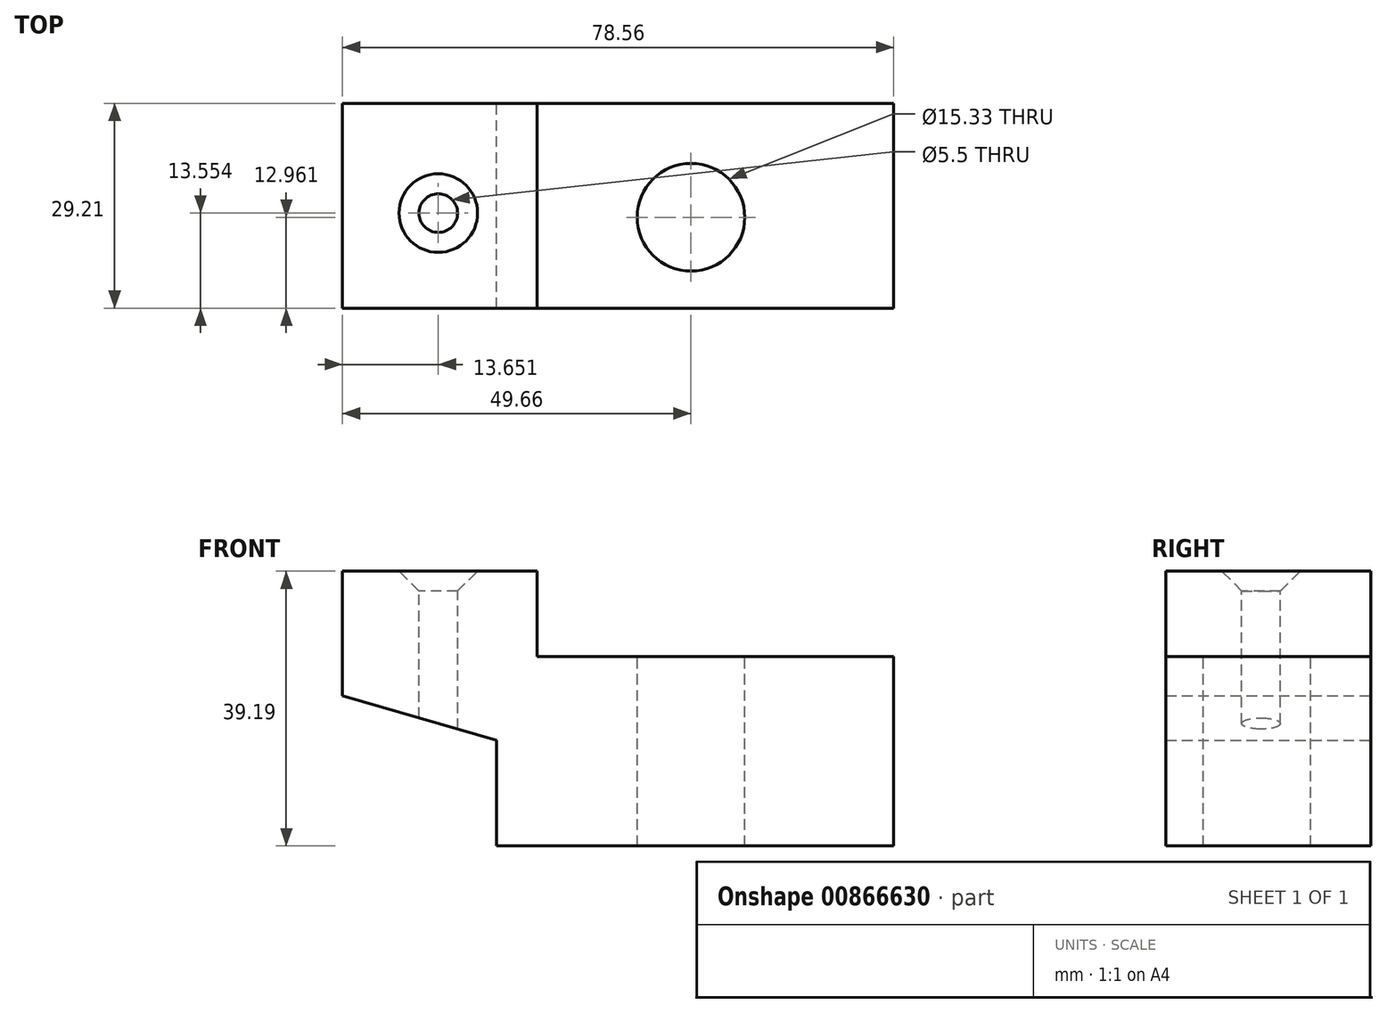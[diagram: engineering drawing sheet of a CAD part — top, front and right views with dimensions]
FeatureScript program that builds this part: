
annotation { "Feature Type Name" : "Feature", "Feature Type Description" : "" }
export const myFeature = defineFeature(function(context is Context, id is Id, definition is map)
    precondition{}
    {
        {
            var Q0;
            Q0=qCreatedBy(makeId("Front.planeOp"),FACE);
            var sketch = newSketch(context, id + "F0", { "sketchPlane" : qUnion([Q0])});
            skLineSegment(sketch, "E0", {"start": v(-42, 8.07) * mm, "end": v(-42, 25.85) * mm});
            skLineSegment(sketch, "E1", {"start": v(-42, 25.85) * mm, "end": v(-14.24, 25.85) * mm});
            skLineSegment(sketch, "E2", {"start": v(-14.24, 25.85) * mm, "end": v(-14.24, 13.7) * mm});
            skLineSegment(sketch, "E3", {"start": v(-14.24, 13.7) * mm, "end": v(36.56, 13.7) * mm});
            skLineSegment(sketch, "E4", {"start": v(36.56, 13.7) * mm, "end": v(36.56, -13.34) * mm});
            skLineSegment(sketch, "E5", {"start": v(36.56, -13.34) * mm, "end": v(-20.05, -13.34) * mm});
            skLineSegment(sketch, "E6", {"start": v(-20.05, -13.34) * mm, "end": v(-20.05, 1.72) * mm});
            skLineSegment(sketch, "E7", {"start": v(-20.05, 1.72) * mm, "end": v(-42, 8.07) * mm});
            skSolve(sketch);
        }
        {
            var Q0;
            Q0 = qSketchRegion(id + "F0", true);
            extrude(context, id + "F1", {"entities" : qUnion([Q0]), "depth" : 29.2 * mm, "offsetDistance" : 25.4 * mm});
        }
        {
            var Q0;
            Q0=makeQuery(id+"F1.opExtrude","SWEPT_FACE",FACE,{"disambiguationData":[OSD([sQuery(id+"F0.wireOp",EDGE,"E3")])]});
            var sketch = newSketch(context, id + "F2", { "sketchPlane" : qUnion([Q0])});
            skCircle(sketch, "E8", {"center": v(7.66, -16.25) * mm, "radius": 7.66 * mm});
            skSolve(sketch);
        }
        {
            var Q0;
            Q0 = qSketchRegion(id + "F2", true);
            extrude(context, id + "F3", {"entities" : qUnion([Q0]), "operationType" : NewBodyOperationType.REMOVE, "oppositeDirection" : true, "depth" : 41.4 * mm, "offsetDistance" : 25.4 * mm});
        }
        {
            var Q0;
            Q0=makeQuery(id+"F1.opExtrude","SWEPT_FACE",FACE,{"disambiguationData":[OSD([sQuery(id+"F0.wireOp",EDGE,"E1")])]});
            var sketch = newSketch(context, id + "F4", { "sketchPlane" : qUnion([Q0])});
            skPoint(sketch, "E9", {"position": v(-28.35, -15.66) * mm});
            skSolve(sketch);
        }
        {
            var Q0;
            Q0=sQuery(id+"F4.wireOp",VERTEX,"E9");
            var Q1;
            Q1=makeQuery(id+"F1.opExtrude","SWEPT_BODY",BODY,{"disambiguationData":[OSD([sQuery(id+"F0.wireOp",EDGE,"E0"),sQuery(id+"F0.wireOp",EDGE,"E1"),sQuery(id+"F0.wireOp",EDGE,"E2"),sQuery(id+"F0.wireOp",EDGE,"E3"),sQuery(id+"F0.wireOp",EDGE,"E4"),sQuery(id+"F0.wireOp",EDGE,"E5"),sQuery(id+"F0.wireOp",EDGE,"E6"),sQuery(id+"F0.wireOp",EDGE,"E7")])]});
            hole(context, id + "F5", {"style" : HoleStyle.C_SINK, "endStyle" : HoleEndStyle.THROUGH, "standardTappedOrClearance" : lookupTablePath({ "fit" : "Normal", "standard" : "ISO", "size" : "M5", "type" : "Clearance" }), "standardBlindInLast" : lookupTablePath({ "fit" : "Standard", "standard" : "ISO", "size" : "M5", "type" : "Clearance" }), "holeDiameter" : 5.5 * mm, "cSinkDiameter" : 11.2 * mm, "cSinkAngle" : 90 * degree, "majorDiameter" : 6.35 * mm, "isTappedThrough" : true, "tappedDepth" : 12.7 * mm, "tapClearance" : 3, "locations" : qUnion([Q0]), "scope" : qUnion([Q1])});
        }
    });
